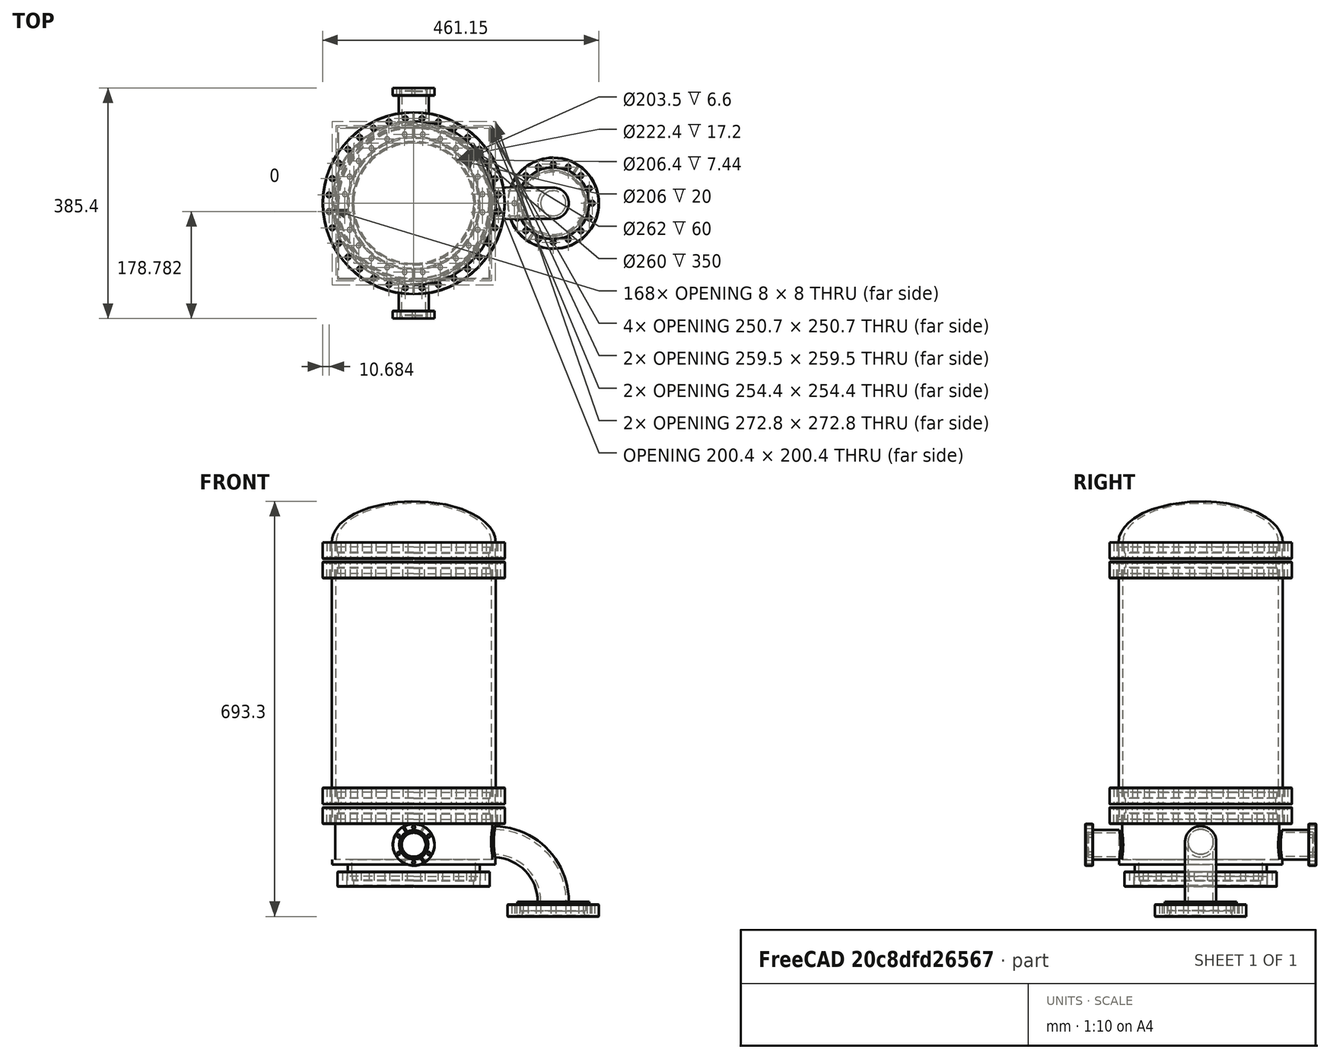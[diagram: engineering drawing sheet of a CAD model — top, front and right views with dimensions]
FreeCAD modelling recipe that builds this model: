
FCSTD DOCUMENT  (FreeCAD 1.0R39285 (Git))
Label: VacuumChamber
License: All rights reserved
LicenseURL: https://en.wikipedia.org/wiki/All_rights_reserved
objects: Part::FeaturePython×18, Part::MultiFuse×15, Part::Feature×10, Part::Cut×8, Part::Mirroring×2, Part::Sphere×2, Part::Scale×2, Part::Torus×2, Part::Cylinder×1
note: 60 computed .brp shape members not serialized (recipe doc carries the construction recipe); baked Part::Feature solids carry a one-line shape summary decoded from their .brp

FEATURE [Part::FeaturePython] Tube  # WARN: FeaturePython — macro-defined, semantics opaque (R4)
  AttacherType = Attacher::AttachEngine3D
  Height = 350
  InnerRadius = 130
  OuterRadius = 137
FEATURE [Part::Feature] Part__Feature  label="190115-1"
  shape: bbox 304 x 27.3 x 304 mm, 318 faces (baked)
FEATURE [Part::Feature] Part__Feature001  label="190115-2"
  Placement = pos=(0,7.6,0) rot=(0,0,1;0rad)
  shape: bbox 276.2 x 19 x 276.2 mm, 17 faces (baked)
FEATURE [Part::MultiFuse] Fusion  label="ere"
  Placement = pos=(0,0,350) rot=(1,0,0;1.5708rad)
  Shapes = -> [Part__Feature,Part__Feature001]
FEATURE [Part::FeaturePython] Tube001  # WARN: FeaturePython — macro-defined, semantics opaque (R4)
  AttacherType = Attacher::AttachEngine3D
  Height = 25
  InnerRadius = 150
  OuterRadius = 152
  Placement = pos=(0,0,351) rot=(0,0,1;0rad)
FEATURE [Part::MultiFuse] Fusion001  label="DN250CF"
  Shapes = -> [Fusion,Tube001]
FEATURE [Part::Mirroring] Part__Mirroring  label="DN250CF (Mirror #1)"
  Base = (0,0,0)
  Normal = (0,0,1)
  Placement = pos=(0,0,350) rot=(0,0,1;0rad)
  Source = -> Fusion001
FEATURE [Part::MultiFuse] Fusion002  label="VacuumChamber"
  Shapes = -> [Part__Mirroring,Fusion001,Tube]
FEATURE [Part::Sphere] Sphere
  Angle1 = -90
  Angle2 = 90
  Angle3 = 180
  AttacherType = Attacher::AttachEngine3D
  Placement = pos=(0,0,500) rot=(0,0,1;0rad)
  Radius = 137
FEATURE [Part::Sphere] Sphere001
  Angle1 = -90
  Angle2 = 90
  Angle3 = 180
  AttacherType = Attacher::AttachEngine3D
  Placement = pos=(0,0,500) rot=(0,0,1;0rad)
  Radius = 130
FEATURE [Part::Scale] Scale
  Base = -> Sphere
  Uniform = false
  UniformScale = 1
  XScale = 1
  YScale = 0.5
  ZScale = 1
FEATURE [Part::Scale] Scale001
  Base = -> Sphere001
  Uniform = false
  UniformScale = 1
  XScale = 1
  YScale = 0.5
  ZScale = 1
FEATURE [Part::Cut] Cut
  Base = -> Scale
  Placement = pos=(0,0,450) rot=(1,0,0;1.5708rad)
  Tool = -> Scale001
FEATURE [Part::Feature] Part__Feature002  label="190115-003"
  shape: bbox 304 x 27.3 x 304 mm, 318 faces (baked)
FEATURE [Part::Feature] Part__Feature003  label="190115-004"
  Placement = pos=(0,7.6,0) rot=(0,0,1;0rad)
  shape: bbox 276.2 x 19 x 276.2 mm, 17 faces (baked)
FEATURE [Part::MultiFuse] Fusion003  label="ere001"
  Placement = pos=(0,0,350) rot=(1,0,0;1.5708rad)
  Shapes = -> [Part__Feature002,Part__Feature003]
FEATURE [Part::FeaturePython] Tube002  # WARN: FeaturePython — macro-defined, semantics opaque (R4)
  AttacherType = Attacher::AttachEngine3D
  Height = 25
  InnerRadius = 150
  OuterRadius = 152
  Placement = pos=(0,0,351) rot=(0,0,1;0rad)
FEATURE [Part::MultiFuse] Fusion004  label="DN250CF001"
  Shapes = -> [Fusion003,Tube002]
FEATURE [Part::Mirroring] Part__Mirroring001  label="DN250CF (Mirror #1)001"
  Base = (0,0,0)
  Normal = (0,0,1)
  Placement = pos=(0,0,800) rot=(0,0,1;0rad)
  Source = -> Fusion004
FEATURE [Part::MultiFuse] Fusion005  label="Cap1"
  Placement = pos=(0,0,-40) rot=(0,0,1;0rad)
  Shapes = -> [Cut,Part__Mirroring001]
FEATURE [Part::Feature] Part__Feature004  label="190115-005"
  shape: bbox 304 x 27.3 x 304 mm, 318 faces (baked)
FEATURE [Part::Feature] Part__Feature005  label="190115-006"
  Placement = pos=(0,7.6,0) rot=(0,0,1;0rad)
  shape: bbox 276.2 x 19 x 276.2 mm, 17 faces (baked)
FEATURE [Part::MultiFuse] Fusion006  label="ere002"
  Placement = pos=(0,0,350) rot=(1,0,0;1.5708rad)
  Shapes = -> [Part__Feature004,Part__Feature005]
FEATURE [Part::FeaturePython] Tube003  # WARN: FeaturePython — macro-defined, semantics opaque (R4)
  AttacherType = Attacher::AttachEngine3D
  Height = 25
  InnerRadius = 150
  OuterRadius = 152
  Placement = pos=(0,0,351) rot=(0,0,1;0rad)
FEATURE [Part::MultiFuse] Fusion007  label="DN250CF002"
  Placement = pos=(0,0,-410) rot=(0,0,1;0rad)
  Shapes = -> [Fusion006,Tube003]
FEATURE [Part::Feature] Part__Feature1456  label="InletFlange"
  Placement = pos=(0,0,-140) rot=(1,0,0;4.71239rad)
  shape: bbox 254 x 254 x 24.64 mm, 51 faces (baked)
FEATURE [Part::FeaturePython] Tube004  # WARN: FeaturePython — macro-defined, semantics opaque (R4)
  AttacherType = Attacher::AttachEngine3D
  Height = 20
  InnerRadius = 103
  OuterRadius = 110
  Placement = pos=(0,0,-140) rot=(0,0,1;0rad)
FEATURE [Part::FeaturePython] Tube005  # WARN: FeaturePython — macro-defined, semantics opaque (R4)
  AttacherType = Attacher::AttachEngine3D
  Height = 8
  InnerRadius = 110
  OuterRadius = 136
  Placement = pos=(0,0,-128) rot=(0,0,1;0rad)
FEATURE [Part::Feature] Part__Feature1457  label="wh"
  Placement = pos=(0,0,0) rot=(1,0,0;1.5708rad)
  shape: bbox 69.9 x 69.9 x 12.7 mm, 278 faces (baked)
FEATURE [Part::FeaturePython] Tube006  # WARN: FeaturePython — macro-defined, semantics opaque (R4)
  AttacherType = Attacher::AttachEngine3D
  Height = 10.5
  InnerRadius = 32
  OuterRadius = 34.95
  Placement = pos=(0,0,1) rot=(0,0,1;0rad)
FEATURE [Part::MultiFuse] Fusion009  label="PreIGP"
  Placement = pos=(0,180,-95) rot=(1,0,0;4.71239rad)
  Shapes = -> [Part__Feature1457,Tube006]
FEATURE [Part::FeaturePython] Tube007  # WARN: FeaturePython — macro-defined, semantics opaque (R4)
  AttacherType = Attacher::AttachEngine3D
  Height = 48
  InnerRadius = 20
  OuterRadius = 25
  Placement = pos=(0,180,-95) rot=(1,0,0;1.5708rad)
FEATURE [Part::Feature] Part__Feature1459  label="190094"
  shape: bbox 152.3 x 19.8 x 152.3 mm, 298 faces (baked)
FEATURE [Part::FeaturePython] Tube010  # WARN: FeaturePython — macro-defined, semantics opaque (R4)
  AttacherType = Attacher::AttachEngine3D
  Height = 18
  InnerRadius = 74
  OuterRadius = 76.15
  Placement = pos=(0,19,0) rot=(1,0,0;1.5708rad)
FEATURE [Part::MultiFuse] Fusion013  label="BAFlange"
  Placement = pos=(0,25,0) rot=(0,0,1;0rad)
  Shapes = -> [Part__Feature1459,Tube010]
FEATURE [Part::FeaturePython] Tube011  # WARN: FeaturePython — macro-defined, semantics opaque (R4)
  AttacherType = Attacher::AttachEngine3D
  Height = 5
  InnerRadius = 21
  OuterRadius = 60
  Placement = pos=(0,25,0) rot=(1,0,0;1.5708rad)
FEATURE [Part::MultiFuse] Fusion014  label="BA_Flange"
  Placement = pos=(233,0,-170) rot=(1,0,0;4.71239rad)
  Shapes = -> [Tube011,Fusion013]
FEATURE [Part::FeaturePython] Tube012  # WARN: FeaturePython — macro-defined, semantics opaque (R4)
  AttacherType = Attacher::AttachEngine3D
  Height = 60
  InnerRadius = 131
  OuterRadius = 136
  Placement = pos=(0,0,-120) rot=(0,0,1;0rad)
FEATURE [Part::FeaturePython] Tube013  # WARN: FeaturePython — macro-defined, semantics opaque (R4)
  AttacherType = Attacher::AttachEngine3D
  Height = 48
  InnerRadius = 0
  OuterRadius = 20
  Placement = pos=(0,150,-95) rot=(1,0,0;1.5708rad)
FEATURE [Part::Cut] Cut001
  Base = -> Tube012
  Tool = -> Tube013
FEATURE [Part::FeaturePython] Tube014  # WARN: FeaturePython — macro-defined, semantics opaque (R4)
  AttacherType = Attacher::AttachEngine3D
  Height = 48
  InnerRadius = 0
  OuterRadius = 20
  Placement = pos=(0,-110,-95) rot=(1,0,0;1.5708rad)
FEATURE [Part::Cut] Cut002
  Base = -> Cut001
  Tool = -> Tube014
FEATURE [Part::FeaturePython] Tube015  # WARN: FeaturePython — macro-defined, semantics opaque (R4)
  AttacherType = Attacher::AttachEngine3D
  Height = 60
  InnerRadius = 0
  OuterRadius = 136
  Placement = pos=(0,0,-120) rot=(0,0,1;0rad)
FEATURE [Part::Cut] Cut003
  Base = -> Tube007
  Tool = -> Tube015
FEATURE [Part::MultiFuse] Fusion015  label="IGP_Flange"
  Shapes = -> [Cut003,Fusion009]
FEATURE [Part::Feature] Part__Feature1460  label="wh001"
  Placement = pos=(0,0,0) rot=(1,0,0;1.5708rad)
  shape: bbox 69.9 x 69.9 x 12.7 mm, 278 faces (baked)
FEATURE [Part::FeaturePython] Tube016  # WARN: FeaturePython — macro-defined, semantics opaque (R4)
  AttacherType = Attacher::AttachEngine3D
  Height = 10.5
  InnerRadius = 32
  OuterRadius = 34.95
  Placement = pos=(0,0,1) rot=(0,0,1;0rad)
FEATURE [Part::MultiFuse] Fusion016  label="PreIGP001"
  Placement = pos=(0,180,-95) rot=(1,0,0;4.71239rad)
  Shapes = -> [Part__Feature1460,Tube016]
FEATURE [Part::FeaturePython] Tube017  # WARN: FeaturePython — macro-defined, semantics opaque (R4)
  AttacherType = Attacher::AttachEngine3D
  Height = 48
  InnerRadius = 20
  OuterRadius = 25
  Placement = pos=(0,180,-95) rot=(1,0,0;1.5708rad)
FEATURE [Part::FeaturePython] Tube018  # WARN: FeaturePython — macro-defined, semantics opaque (R4)
  AttacherType = Attacher::AttachEngine3D
  Height = 60
  InnerRadius = 0
  OuterRadius = 136
  Placement = pos=(0,0,-120) rot=(0,0,1;0rad)
FEATURE [Part::Cut] Cut004
  Base = -> Tube017
  Tool = -> Tube018
FEATURE [Part::MultiFuse] Fusion017  label="RotaryVane_Flange"
  Placement = pos=(0,0,0) rot=(0,0,1;3.14159rad)
  Shapes = -> [Cut004,Fusion016]
FEATURE [Part::Torus] Torus
  Angle1 = -180
  Angle2 = 180
  Angle3 = 90
  AttacherType = Attacher::AttachEngine3D
  Placement = pos=(400,0,0) rot=(1,0,0;1.5708rad)
  Radius1 = 100
  Radius2 = 26
FEATURE [Part::Torus] Torus001
  Angle1 = -180
  Angle2 = 180
  Angle3 = 90
  AttacherType = Attacher::AttachEngine3D
  Placement = pos=(400,0,0) rot=(1,0,0;1.5708rad)
  Radius1 = 100
  Radius2 = 21
FEATURE [Part::Cut] Cut005
  Base = -> Torus
  Placement = pos=(-267,0,-190) rot=(0,0,1;0rad)
  Tool = -> Torus001
FEATURE [Part::FeaturePython] Tube019  # WARN: FeaturePython — macro-defined, semantics opaque (R4)
  AttacherType = Attacher::AttachEngine3D
  Height = 60
  InnerRadius = 0
  OuterRadius = 136
  Placement = pos=(0,0,-120) rot=(0,0,1;0rad)
FEATURE [Part::Cut] Cut006
  Base = -> Cut005
  Tool = -> Tube019
FEATURE [Part::Cylinder] Cylinder
  Angle = 360
  AttacherType = Attacher::AttachEngine3D
  FirstAngle = 0
  Height = 40
  Placement = pos=(103,0,-90) rot=(0,1,0;1.5708rad)
  Radius = 21
  SecondAngle = 0
FEATURE [Part::Cut] Cut007
  Base = -> Cut002
  Tool = -> Cylinder
FEATURE [Part::MultiFuse] Fusion018  label="FlangedBottoms"
  Shapes = -> [Cut007,Cut006,Fusion017,Fusion014,Fusion015,Tube005,Tube004,Part__Feature1456,Fusion007]
